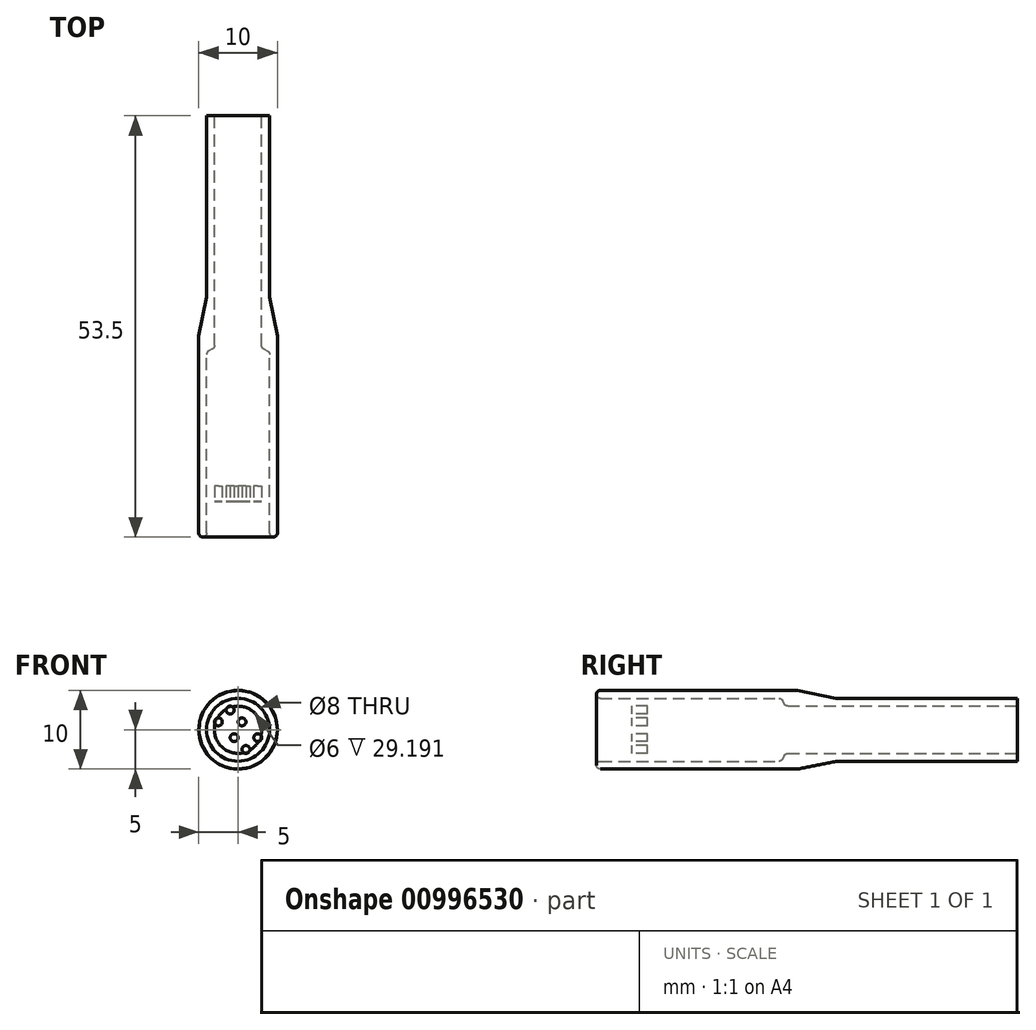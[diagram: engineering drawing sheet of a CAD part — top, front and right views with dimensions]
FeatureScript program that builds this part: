
annotation { "Feature Type Name" : "Feature", "Feature Type Description" : "" }
export const myFeature = defineFeature(function(context is Context, id is Id, definition is map)
    precondition{}
    {
        {
            var Q0;
            Q0=qCreatedBy(makeId("Right.planeOp"),FACE);
            var sketch = newSketch(context, id + "F0", { "sketchPlane" : qUnion([Q0])});
            skLineSegment(sketch, "E0.bottom", {"start": v(-12.5, 5) * mm, "end": v(13.5, 5) * mm});
            skLineSegment(sketch, "E0.top", {"start": v(-12.5, -5) * mm, "end": v(13.5, -5) * mm});
            skLineSegment(sketch, "E0.left", {"start": v(-12.5, 5) * mm, "end": v(-12.5, -5) * mm});
            skLineSegment(sketch, "E0.right", {"start": v(13.5, 5) * mm, "end": v(13.5, -5) * mm});
            skLineSegment(sketch, "E1.bottom", {"start": v(13.5, 4) * mm, "end": v(41.5, 4) * mm});
            skLineSegment(sketch, "E1.top", {"start": v(13.5, -4) * mm, "end": v(41.5, -4) * mm});
            skLineSegment(sketch, "E1.left", {"start": v(13.5, 4) * mm, "end": v(13.5, -4) * mm});
            skLineSegment(sketch, "E1.right", {"start": v(41.5, 4) * mm, "end": v(41.5, -4) * mm});
            skLineSegment(sketch, "E2", {"start": v(41.5, 0) * mm, "end": v(-12.5, 0) * mm});
            skLineSegment(sketch, "E3.bottom", {"start": v(-12.5, 4) * mm, "end": v(12.5, 4) * mm});
            skLineSegment(sketch, "E3.top", {"start": v(-12.5, -4) * mm, "end": v(12.5, -4) * mm});
            skLineSegment(sketch, "E3.left", {"start": v(-12.5, 4) * mm, "end": v(-12.5, -4) * mm});
            skLineSegment(sketch, "E3.right", {"start": v(12.5, 4) * mm, "end": v(12.5, -4) * mm});
            skLineSegment(sketch, "E4.bottom", {"start": v(12.5, 3) * mm, "end": v(41.5, 3) * mm});
            skLineSegment(sketch, "E4.top", {"start": v(12.5, -3) * mm, "end": v(41.5, -3) * mm});
            skLineSegment(sketch, "E4.left", {"start": v(12.5, 3) * mm, "end": v(12.5, -3) * mm});
            skLineSegment(sketch, "E4.right", {"start": v(41.5, 3) * mm, "end": v(41.5, -3) * mm});
            skLineSegment(sketch, "E5", {"start": v(-7.5, 4) * mm, "end": v(-7.5, 0) * mm});
            skLineSegment(sketch, "E6.bottom", {"start": v(-7.5, 0) * mm, "end": v(-5.5, 0) * mm});
            skLineSegment(sketch, "E6.top", {"start": v(-7.5, 4) * mm, "end": v(-5.5, 4) * mm});
            skLineSegment(sketch, "E6.left", {"start": v(-7.5, 0) * mm, "end": v(-7.5, 4) * mm});
            skLineSegment(sketch, "E6.right", {"start": v(-5.5, 0) * mm, "end": v(-5.5, 4) * mm});
            skSolve(sketch);
        }
        {
            var Q0;
            {var subQ1=sQuery(id+"F0.wireOp",EDGE,"E0.bottom");Q0=makeQuery(id+"F0.imprint","IMPRINT",FACE,{"disambiguationData":[TD([[makeQuery(id+"F0.imprint","IMPRINT",EDGE,{"derivedFrom":subQ1}),-1.0]])]});}
            var Q1;
            {var subQ3=sQuery(id+"F0.wireOp",EDGE,"E1.bottom");Q1=makeQuery(id+"F0.imprint","IMPRINT",FACE,{"disambiguationData":[TD([[makeQuery(id+"F0.imprint","IMPRINT",EDGE,{"derivedFrom":subQ3}),-1.0]])]});}
            var Q2;
            Q2=sQuery(id+"F0.wireOp",EDGE,"E2");
            revolve(context, id + "F1", {"surfaceOperationType" : NewSurfaceOperationType.NEW, "entities" : qUnion([Q0, Q1]), "axis" : qUnion([Q2]), "revolveType" : RevolveType.FULL});
        }
        {
            var Q0;
            {var subQ0=sQuery(id+"F0.wireOp",EDGE,"E5");Q0=makeQuery(id+"F0.imprint","IMPRINT",FACE,{"disambiguationData":[TD([[makeQuery(id+"F0.imprint","IMPRINT",EDGE,{"derivedFrom":subQ0}),1.0]])]});}
            var Q1;
            Q1=sQuery(id+"F0.wireOp",EDGE,"E2");
            revolve(context, id + "F2", {"surfaceOperationType" : NewSurfaceOperationType.NEW, "entities" : qUnion([Q0]), "axis" : qUnion([Q1]), "revolveType" : RevolveType.FULL});
        }
        {
            var Q0;
            Q0=makeQuery(id+"F1.opRevolve","SWEPT_EDGE",EDGE,{"disambiguationData":[OSD([sQuery(id+"F0.wireOp",EDGE,"E0.right"),sQuery(id+"F0.wireOp",EDGE,"E1.bottom")])]});
            chamfer(context, id + "F3", {"entities" : qUnion([Q0]), "chamferType" : ChamferType.TWO_OFFSETS, "width1" : 1 * mm, "oppositeDirection" : true, "width2" : 5 * mm, "tangentPropagation" : true});
        }
        {
            var Q0;
            Q0=makeQuery(id+"F1.opRevolve","SWEPT_EDGE",EDGE,{"disambiguationData":[OSD([sQuery(id+"F0.wireOp",EDGE,"E0.bottom"),sQuery(id+"F0.wireOp",EDGE,"E0.left")])]});
            fillet(context, id + "F4", {"entities" : qUnion([Q0]), "radius" : 1 * mm, "tangentPropagation" : true, "allowEdgeOverflow" : false});
        }
        {
            var Q0;
            Q0=makeQuery(id+"F4.opFillet","BLEND_EDGE",EDGE,{"blendedFrom":[makeQuery(id+"F1.opRevolve","SWEPT_EDGE",EDGE,{"disambiguationData":[OSD([sQuery(id+"F0.wireOp",EDGE,"E0.bottom"),sQuery(id+"F0.wireOp",EDGE,"E0.left")])]}),makeQuery(id+"F1.opRevolve","SWEPT_FACE",FACE,{"disambiguationData":[OSD([sQuery(id+"F0.wireOp",EDGE,"E3.bottom")])]})],"blendedInto":[makeQuery(id+"F1.opRevolve","SWEPT_FACE",FACE,{"disambiguationData":[OSD([sQuery(id+"F0.wireOp",EDGE,"E3.bottom")])]})]});
            fillet(context, id + "F5", {"entities" : qUnion([Q0]), "radius" : 0.5 * mm, "tangentPropagation" : true, "allowEdgeOverflow" : false});
        }
        {
            var Q0;
            Q0=makeQuery(id+"F1.opRevolve","SWEPT_EDGE",EDGE,{"disambiguationData":[OSD([sQuery(id+"F0.wireOp",EDGE,"E3.bottom"),sQuery(id+"F0.wireOp",EDGE,"E3.right")])]});
            chamfer(context, id + "F6", {"entities" : qUnion([Q0]), "chamferType" : ChamferType.TWO_OFFSETS, "width1" : 1 * mm, "oppositeDirection" : false, "width2" : 2 * mm, "tangentPropagation" : true});
        }
        {
            var Q0;
            Q0=makeQuery(id+"F2.opRevolve","SWEPT_FACE",FACE,{"disambiguationData":[OSD([sQuery(id+"F0.wireOp",EDGE,"E5")])]});
            var sketch = newSketch(context, id + "F7", { "sketchPlane" : qUnion([Q0])});
            skCircle(sketch, "E7", {"center": v(1, 2.5) * mm, "radius": 0.5 * mm});
            skCircle(sketch, "E8", {"center": v(2.5, 1) * mm, "radius": 0.5 * mm});
            skCircle(sketch, "E9.MirrorC", {"center": v(2.5, -1) * mm, "radius": 0.5 * mm});
            skCircle(sketch, "E10.MirrorC", {"center": v(1, -2.5) * mm, "radius": 0.5 * mm});
            skLineSegment(sketch, "E11.bottom", {"start": v(1.5, -1.5) * mm, "end": v(-1.5, -1.5) * mm});
            skLineSegment(sketch, "E11.top", {"start": v(1.5, 1.5) * mm, "end": v(-1.5, 1.5) * mm});
            skLineSegment(sketch, "E11.left", {"start": v(1.5, -1.5) * mm, "end": v(1.5, 1.5) * mm});
            skLineSegment(sketch, "E11.right", {"start": v(-1.5, -1.5) * mm, "end": v(-1.5, 1.5) * mm});
            skPoint(sketch, "E11.middle", {"position": v(0, 0) * mm});
            skCircle(sketch, "E12.MirrorC", {"center": v(0.5, 1) * mm, "radius": 0.5 * mm});
            skCircle(sketch, "E13.MirrorC", {"center": v(1, -0.5) * mm, "radius": 0.5 * mm});
            skCircle(sketch, "E14.MirrorC", {"center": v(-1, 2.5) * mm, "radius": 0.5 * mm});
            skCircle(sketch, "E15.MirrorC", {"center": v(-2.5, 1) * mm, "radius": 0.5 * mm});
            skCircle(sketch, "E16.MirrorC", {"center": v(-2.5, -1) * mm, "radius": 0.5 * mm});
            skCircle(sketch, "E17.MirrorC", {"center": v(-1, -2.5) * mm, "radius": 0.5 * mm});
            skCircle(sketch, "E18.MirrorC", {"center": v(-0.5, -1) * mm, "radius": 0.5 * mm});
            skCircle(sketch, "E19.MirrorC", {"center": v(-1, 0.5) * mm, "radius": 0.5 * mm});
            skSolve(sketch);
        }
        {
            var Q0;
            Q0=makeQuery(id+"F7.imprint","IMPRINT",FACE,{"disambiguationData":[TD([[makeQuery(id+"F7.imprint","IMPRINT",EDGE,{"derivedFrom":sQuery(id+"F7.wireOp",EDGE,"E15.MirrorC")}),-1.0]])]});
            var Q1;
            Q1=makeQuery(id+"F7.imprint","IMPRINT",FACE,{"disambiguationData":[TD([[makeQuery(id+"F7.imprint","IMPRINT",EDGE,{"derivedFrom":sQuery(id+"F7.wireOp",EDGE,"E14.MirrorC")}),-1.0]])]});
            var Q2;
            Q2=makeQuery(id+"F7.imprint","IMPRINT",FACE,{"disambiguationData":[TD([[makeQuery(id+"F7.imprint","IMPRINT",EDGE,{"derivedFrom":sQuery(id+"F7.wireOp",EDGE,"E7")}),1.0]])]});
            var Q3;
            Q3=makeQuery(id+"F7.imprint","IMPRINT",FACE,{"disambiguationData":[TD([[makeQuery(id+"F7.imprint","IMPRINT",EDGE,{"derivedFrom":sQuery(id+"F7.wireOp",EDGE,"E19.MirrorC")}),1.0]])]});
            var Q4;
            Q4=makeQuery(id+"F7.imprint","IMPRINT",FACE,{"disambiguationData":[TD([[makeQuery(id+"F7.imprint","IMPRINT",EDGE,{"derivedFrom":sQuery(id+"F7.wireOp",EDGE,"E12.MirrorC")}),-1.0]])]});
            var Q5;
            Q5=makeQuery(id+"F7.imprint","IMPRINT",FACE,{"disambiguationData":[TD([[makeQuery(id+"F7.imprint","IMPRINT",EDGE,{"derivedFrom":sQuery(id+"F7.wireOp",EDGE,"E8")}),1.0]])]});
            var Q6;
            Q6=makeQuery(id+"F7.imprint","IMPRINT",FACE,{"disambiguationData":[TD([[makeQuery(id+"F7.imprint","IMPRINT",EDGE,{"derivedFrom":sQuery(id+"F7.wireOp",EDGE,"E9.MirrorC")}),-1.0]])]});
            var Q7;
            Q7=makeQuery(id+"F7.imprint","IMPRINT",FACE,{"disambiguationData":[TD([[makeQuery(id+"F7.imprint","IMPRINT",EDGE,{"derivedFrom":sQuery(id+"F7.wireOp",EDGE,"E13.MirrorC")}),1.0]])]});
            var Q8;
            Q8=makeQuery(id+"F7.imprint","IMPRINT",FACE,{"disambiguationData":[TD([[makeQuery(id+"F7.imprint","IMPRINT",EDGE,{"derivedFrom":sQuery(id+"F7.wireOp",EDGE,"E18.MirrorC")}),-1.0]])]});
            var Q9;
            Q9=makeQuery(id+"F7.imprint","IMPRINT",FACE,{"disambiguationData":[TD([[makeQuery(id+"F7.imprint","IMPRINT",EDGE,{"derivedFrom":sQuery(id+"F7.wireOp",EDGE,"E17.MirrorC")}),1.0]])]});
            var Q10;
            Q10=makeQuery(id+"F7.imprint","IMPRINT",FACE,{"disambiguationData":[TD([[makeQuery(id+"F7.imprint","IMPRINT",EDGE,{"derivedFrom":sQuery(id+"F7.wireOp",EDGE,"E10.MirrorC")}),-1.0]])]});
            var Q11;
            Q11=makeQuery(id+"F7.imprint","IMPRINT",FACE,{"disambiguationData":[TD([[makeQuery(id+"F7.imprint","IMPRINT",EDGE,{"derivedFrom":sQuery(id+"F7.wireOp",EDGE,"E16.MirrorC")}),1.0]])]});
            extrude(context, id + "F8", {"entities" : qUnion([Q0, Q1, Q2, Q3, Q4, Q5, Q6, Q7, Q8, Q9, Q10, Q11]), "operationType" : NewBodyOperationType.REMOVE, "oppositeDirection" : true, "depth" : 5 * mm, "offsetDistance" : 25 * mm});
        }
        {
            var Q0;
            Q0=makeQuery(id+"F6.opChamfer","BLEND_EDGE",EDGE,{"blendedFrom":[makeQuery(id+"F1.opRevolve","SWEPT_EDGE",EDGE,{"disambiguationData":[OSD([sQuery(id+"F0.wireOp",EDGE,"E3.bottom"),sQuery(id+"F0.wireOp",EDGE,"E3.right")])]}),makeQuery(id+"F1.opRevolve","SWEPT_FACE",FACE,{"disambiguationData":[OSD([sQuery(id+"F0.wireOp",EDGE,"E4.bottom")])]})],"blendedInto":[makeQuery(id+"F1.opRevolve","SWEPT_FACE",FACE,{"disambiguationData":[OSD([sQuery(id+"F0.wireOp",EDGE,"E4.bottom")])]})]});
            var Q1;
            {var subQ0=sQuery(id+"F0.wireOp",EDGE,"E3.bottom");Q1=makeQuery(id+"F6.opChamfer","BLEND_EDGE",EDGE,{"blendedFrom":[makeQuery(id+"F1.opRevolve","SWEPT_EDGE",EDGE,{"disambiguationData":[OSD([subQ0,sQuery(id+"F0.wireOp",EDGE,"E3.right")])]}),makeQuery(id+"F1.opRevolve","SWEPT_FACE",FACE,{"disambiguationData":[OSD([subQ0])]})],"blendedInto":[makeQuery(id+"F1.opRevolve","SWEPT_FACE",FACE,{"disambiguationData":[OSD([subQ0])]})]});}
            var Q2;
            Q2=makeQuery(id+"F3.opChamfer","BLEND_EDGE",EDGE,{"blendedFrom":[makeQuery(id+"F1.opRevolve","SWEPT_EDGE",EDGE,{"disambiguationData":[OSD([sQuery(id+"F0.wireOp",EDGE,"E0.right"),sQuery(id+"F0.wireOp",EDGE,"E1.bottom")])]}),makeQuery(id+"F1.opRevolve","SWEPT_FACE",FACE,{"disambiguationData":[OSD([sQuery(id+"F0.wireOp",EDGE,"E0.bottom")])]})],"blendedInto":[makeQuery(id+"F1.opRevolve","SWEPT_FACE",FACE,{"disambiguationData":[OSD([sQuery(id+"F0.wireOp",EDGE,"E0.bottom")])]})]});
            var Q3;
            {var subQ0=sQuery(id+"F0.wireOp",EDGE,"E1.bottom");Q3=makeQuery(id+"F3.opChamfer","BLEND_EDGE",EDGE,{"blendedFrom":[makeQuery(id+"F1.opRevolve","SWEPT_EDGE",EDGE,{"disambiguationData":[OSD([sQuery(id+"F0.wireOp",EDGE,"E0.right"),subQ0])]}),makeQuery(id+"F1.opRevolve","SWEPT_FACE",FACE,{"disambiguationData":[OSD([subQ0])]})],"blendedInto":[makeQuery(id+"F1.opRevolve","SWEPT_FACE",FACE,{"disambiguationData":[OSD([subQ0])]})]});}
            fillet(context, id + "F9", {"entities" : qUnion([Q0, Q1, Q2, Q3]), "radius" : 0.5 * mm, "tangentPropagation" : true, "allowEdgeOverflow" : false});
        }
    });
